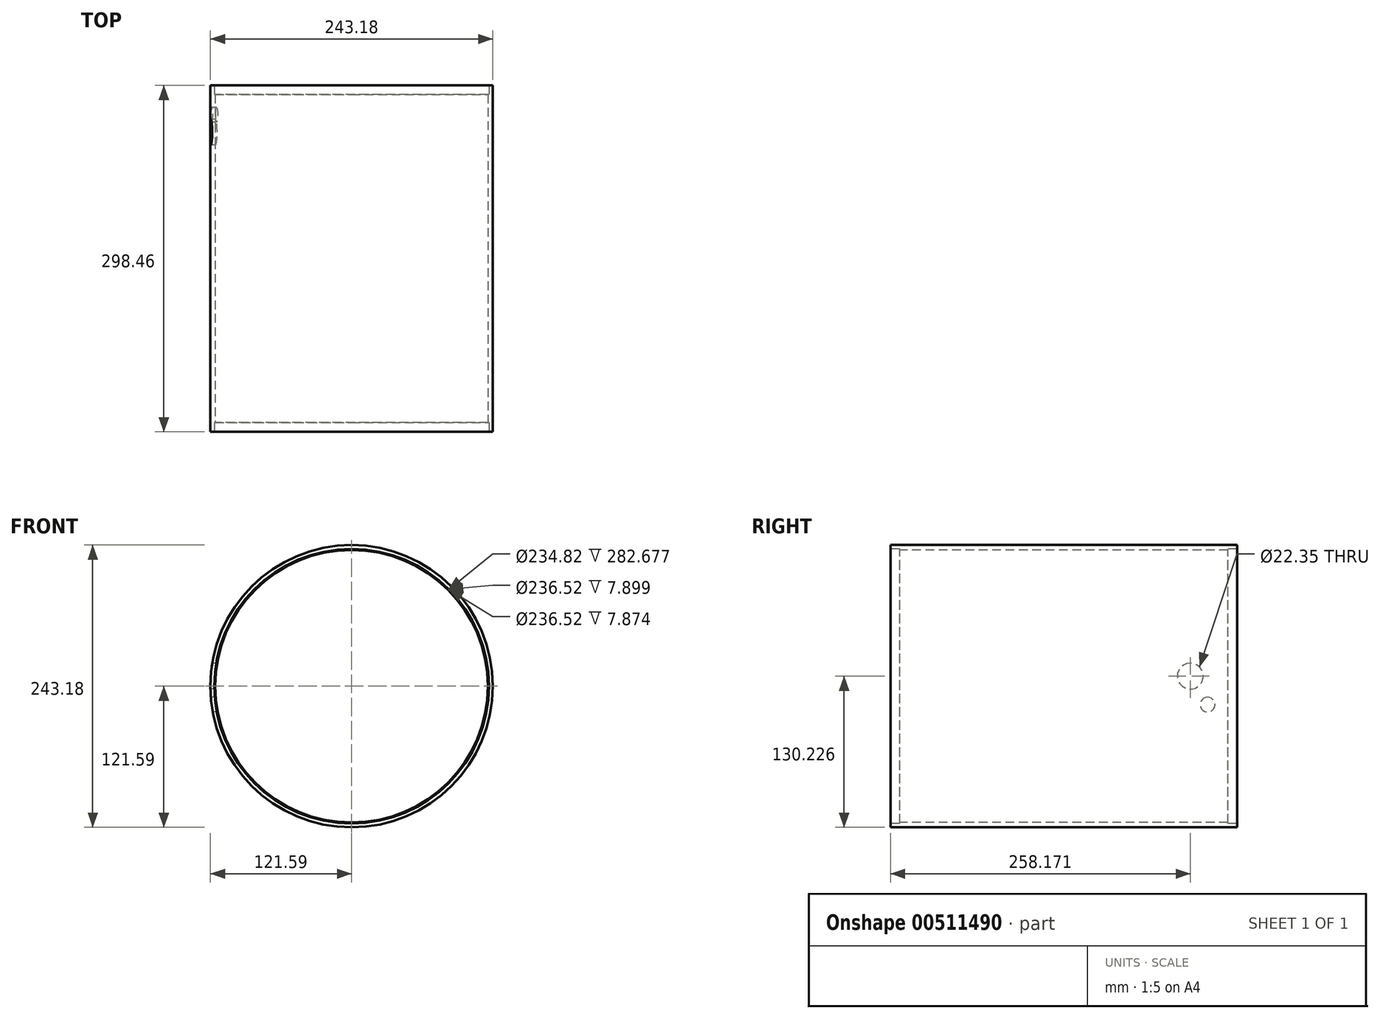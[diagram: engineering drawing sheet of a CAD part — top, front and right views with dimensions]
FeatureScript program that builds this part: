
annotation { "Feature Type Name" : "Feature", "Feature Type Description" : "" }
export const myFeature = defineFeature(function(context is Context, id is Id, definition is map)
    precondition{}
    {
        {
            var Q0;
            Q0=qCreatedBy(makeId("Right.planeOp"),FACE);
            var sketch = newSketch(context, id + "F0", { "sketchPlane" : qUnion([Q0])});
            skLineSegment(sketch, "E0", {"start": v(0, 0) * mm, "end": v(162.31, 0) * mm, "construction": true});
            skLineSegment(sketch, "E1", {"start": v(-149.23, 121.59) * mm, "end": v(149.22, 121.59) * mm});
            skLineSegment(sketch, "E2", {"start": v(149.22, 121.59) * mm, "end": v(149.22, 118.26) * mm});
            skLineSegment(sketch, "E3", {"start": v(149.23, 118.26) * mm, "end": v(141.35, 118.26) * mm});
            skLineSegment(sketch, "E4", {"start": v(141.35, 118.26) * mm, "end": v(141.35, 117.41) * mm});
            skLineSegment(sketch, "E5", {"start": v(141.35, 117.41) * mm, "end": v(-141.33, 117.41) * mm});
            skLineSegment(sketch, "E6", {"start": v(-141.33, 117.41) * mm, "end": v(-141.33, 118.26) * mm});
            skLineSegment(sketch, "E7", {"start": v(-141.33, 118.26) * mm, "end": v(-149.23, 118.26) * mm});
            skLineSegment(sketch, "E8", {"start": v(-149.23, 118.26) * mm, "end": v(-149.23, 121.59) * mm});
            skSolve(sketch);
        }
        {
            var Q0;
            Q0=makeQuery(id+"F0.imprint","IMPRINT",FACE,{"disambiguationData":[TD([[makeQuery(id+"F0.imprint","IMPRINT",EDGE,{"derivedFrom":sQuery(id+"F0.wireOp",EDGE,"E1")}),-1.0]])]});
            var Q1;
            Q1=sQuery(id+"F0.wireOp",EDGE,"E0");
            revolve(context, id + "F1", {"entities" : qUnion([Q0]), "axis" : qUnion([Q1]), "revolveType" : RevolveType.FULL});
        }
        {
            var Q0;
            Q0=makeQuery(id+"F1.opRevolve","SWEPT_FACE",FACE,{"disambiguationData":[OSD([sQuery(id+"F0.wireOp",EDGE,"E8")])]});
            cPlane(context, id + "F2", {"entities" : qUnion([Q0]), "cplaneType" : CPlaneType.OFFSET, "offset" : 38.9 * mm, "oppositeDirection" : true, "width" : 152.4 * mm, "height" : 152.4 * mm});
        }
        {
            var Q0;
            Q0=qCreatedBy(makeId("Right.planeOp"),FACE);
            cPlane(context, id + "F3", {"entities" : qUnion([Q0]), "cplaneType" : CPlaneType.OFFSET, "offset" : 121.64 * mm, "oppositeDirection" : true, "width" : 152.4 * mm, "height" : 152.4 * mm});
        }
        {
            var Q0;
            Q0=qCreatedBy(id+"F3.planeOp",FACE);
            var sketch = newSketch(context, id + "F4", { "sketchPlane" : qUnion([Q0])});
            skLineSegment(sketch, "E9", {"start": v(0, 0) * mm, "end": v(-110.34, 0) * mm, "construction": true});
            skCircle(sketch, "E10", {"center": v(108.94, 8.64) * mm, "radius": 11.18 * mm});
            skCircle(sketch, "E11", {"center": v(123.82, -15.87) * mm, "radius": 6.35 * mm});
            skCircle(sketch, "E12", {"center": v(117.47, 0) * mm, "radius": 17.53 * mm});
            skSolve(sketch);
        }
        {
            var Q0;
            Q0=makeQuery(id+"F4.imprint","IMPRINT",FACE,{"disambiguationData":[TD([[makeQuery(id+"F4.imprint","IMPRINT",EDGE,{"derivedFrom":sQuery(id+"F4.wireOp",EDGE,"E10")}),1.0]])]});
            var Q1;
            Q1=makeQuery(id+"F4.imprint","IMPRINT",FACE,{"disambiguationData":[TD([[makeQuery(id+"F4.imprint","IMPRINT",EDGE,{"derivedFrom":sQuery(id+"F4.wireOp",EDGE,"E11")}),1.0]])]});
            var Q2;
            {var subQ0=sQuery(id+"F4.wireOp",EDGE,"E12");var subQ1=sQuery(id+"F4.wireOp",EDGE,"E10");var subQ2=makeQuery(id+"F4.imprint","INTERSECT",VERTEX,{"disambiguationData":[OD(0.0)],"derivedFrom":[subQ1,subQ0]});Q2=makeQuery(id+"F4.imprint","IMPRINT",FACE,{"disambiguationData":[TD([[makeQuery(id+"F4.imprint","IMPRINT",EDGE,{"disambiguationData":[TD([[subQ2,-1.0]])],"derivedFrom":subQ1}),-1.0]])]});}
            extrude(context, id + "F5", {"entities" : qUnion([Q0, Q1, Q2]), "operationType" : NewBodyOperationType.REMOVE, "depth" : 25.4 * mm, "offsetDistance" : 25.4 * mm});
        }
    });
